FCSTD DOCUMENT  (FreeCAD 0.18R16093 (Git))
Label: ugolok-2d
License: All rights reserved
LicenseURL: http://en.wikipedia.org/wiki/All_rights_reserved
objects: Sketcher::SketchObject×1, PartDesign::Body×1
note: 2 computed .brp shape members not serialized (recipe doc carries the construction recipe); baked Part::Feature solids carry a one-line shape summary decoded from their .brp

FEATURE [Sketcher::SketchObject] Sketch
  MapMode = 5
  Placement = pos=(0,0,0) rot=(1,0,0;1.5708rad)
  Support = -> [XZ_Plane]
  sketch-geometry (14):
    g0: LineSegment StartX=0 StartY=0 StartZ=0 EndX=40 EndY=0 EndZ=0
    g1: LineSegment StartX=40 StartY=0 StartZ=0 EndX=40 EndY=350 EndZ=0
    g2: LineSegment StartX=40 StartY=350 StartZ=0 EndX=0 EndY=350 EndZ=0
    g3: LineSegment StartX=0 StartY=350 StartZ=0 EndX=0 EndY=0 EndZ=0
    g4: LineSegment StartX=0 StartY=350 StartZ=0 EndX=40 EndY=310 EndZ=0
    g5: LineSegment StartX=40 StartY=310 StartZ=0 EndX=310 EndY=310 EndZ=0
    g6: LineSegment StartX=310 StartY=310 StartZ=0 EndX=310 EndY=270 EndZ=0
    g7: LineSegment StartX=310 StartY=270 StartZ=0 EndX=40 EndY=270 EndZ=0
    g8: LineSegment StartX=40 StartY=270 StartZ=0 EndX=40 EndY=310 EndZ=0
    g9: LineSegment StartX=40 StartY=40 StartZ=0 EndX=0 EndY=0 EndZ=0
    g10: LineSegment StartX=270 StartY=270 StartZ=0 EndX=310 EndY=310 EndZ=0
    g11: LineSegment StartX=40 StartY=40 StartZ=0 EndX=270 EndY=270 EndZ=0
    g12: LineSegment StartX=40 StartY=96.5685 StartZ=0 EndX=213.431 EndY=270 EndZ=0
    g13: LineSegment StartX=68.2843 StartY=68.2843 StartZ=0 EndX=40 EndY=96.5685 EndZ=0
  constraints (40):
    c: Coincident(g0,g1)
    c: Coincident(g1,g2)
    c: Coincident(g2,g3)
    c: Coincident(g3,g0)
    c: Horizontal(g0)
    c: Horizontal(g2)
    c: Vertical(g1)
    c: Vertical(g3)
    c: Coincident(g0,g-1)
    c: Distance(g0) = 40
    c: Distance(g3) = 350
    c: PointOnObject(g4,g1)
    c: Coincident(g4,g2)
    c: Angle(g4,g2) = 0.785398
    c: Coincident(g5,g6)
    c: Coincident(g6,g7)
    c: Coincident(g7,g8)
    c: Coincident(g8,g5)
    c: Horizontal(g5)
    c: Horizontal(g7)
    c: Vertical(g6)
    c: Vertical(g8)
    c: Coincident(g5,g4)
    c: Equal(g6,g2)
    c: PointOnObject(g9,g1)
    c: Coincident(g9,g0)
    c: Angle(g0,g9) = 0.785398
    c: PointOnObject(g10,g7)
    c: Coincident(g10,g5)
    c: Angle(g10,g6) = 0.785398
    c: Coincident(g11,g9)
    c: Coincident(g11,g10)
    c: PointOnObject(g12,g1)
    c: PointOnObject(g12,g7)
    c: Parallel(g11,g12)
    c: Angle(g11,g1) = 0.785398
    c: PointOnObject(g13,g11)
    c: Coincident(g13,g12)
    c: Perpendicular(g11,g13)
    c: Equal(g13,g6)
FEATURE [PartDesign::Body] Body
  Group = -> [Sketch]
  Origin = -> Origin
